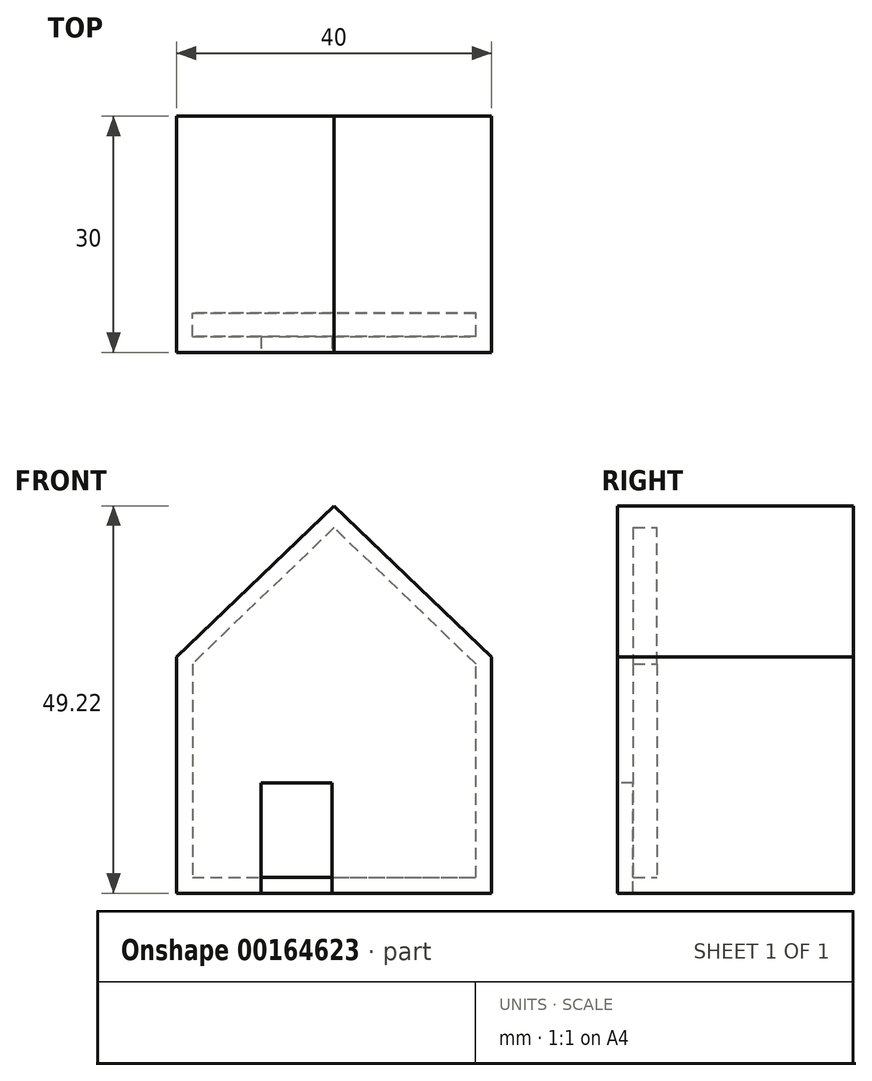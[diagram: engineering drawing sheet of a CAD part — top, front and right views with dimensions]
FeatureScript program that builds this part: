
annotation { "Feature Type Name" : "Feature", "Feature Type Description" : "" }
export const myFeature = defineFeature(function(context is Context, id is Id, definition is map)
    precondition{}
    {
        {
            var Q0;
            Q0=qCreatedBy(makeId("Front.planeOp"),FACE);
            var sketch = newSketch(context, id + "F0", { "sketchPlane" : qUnion([Q0])});
            skLineSegment(sketch, "E0", {"start": v(0, 0) * mm, "end": v(40, 0) * mm});
            skLineSegment(sketch, "E1", {"start": v(40, 0) * mm, "end": v(40, 30) * mm});
            skLineSegment(sketch, "E2", {"start": v(40, 30) * mm, "end": v(20, 49.22) * mm});
            skLineSegment(sketch, "E3", {"start": v(20, 49.22) * mm, "end": v(0, 30) * mm});
            skLineSegment(sketch, "E4", {"start": v(0, 30) * mm, "end": v(0, 0) * mm});
            skSolve(sketch);
        }
        {
            var Q0;
            Q0=makeQuery(id+"F0.imprint","IMPRINT",FACE,{"disambiguationData":[TD([[makeQuery(id+"F0.imprint","IMPRINT",EDGE,{"derivedFrom":sQuery(id+"F0.wireOp",EDGE,"E0")}),1.0]])]});
            extrude(context, id + "F1", {"entities" : qUnion([Q0]), "depth" : 30 * mm});
        }
        {
            var Q0;
            Q0=makeQuery(id+"F1.opExtrude","CAP_FACE",FACE,{"disambiguationData":[OSD([sQuery(id+"F0.wireOp",EDGE,"E0"),sQuery(id+"F0.wireOp",EDGE,"E1"),sQuery(id+"F0.wireOp",EDGE,"E2"),sQuery(id+"F0.wireOp",EDGE,"E3"),sQuery(id+"F0.wireOp",EDGE,"E4")])],"isStart":false});
            var Q1;
            Q1=makeQuery(id+"F1.opExtrude","SWEPT_FACE",FACE,{"disambiguationData":[OSD([sQuery(id+"F0.wireOp",EDGE,"E1")])]});
            var Q2;
            Q2=makeQuery(id+"F1.opExtrude","SWEPT_FACE",FACE,{"disambiguationData":[OSD([sQuery(id+"F0.wireOp",EDGE,"E2")])]});
            var Q3;
            Q3=makeQuery(id+"F1.opExtrude","SWEPT_BODY",BODY,{"disambiguationData":[OSD([sQuery(id+"F0.wireOp",EDGE,"E0"),sQuery(id+"F0.wireOp",EDGE,"E1"),sQuery(id+"F0.wireOp",EDGE,"E2"),sQuery(id+"F0.wireOp",EDGE,"E3"),sQuery(id+"F0.wireOp",EDGE,"E4")])]});
            shell(context, id + "F2", {"isHollow" : true, "entities" : qUnion([Q0, Q1, Q2]), "parts" : qUnion([Q3]), "thickness" : 2 * mm});
        }
        {
            var Q0;
            Q0=makeQuery(id+"F1.opExtrude","CAP_FACE",FACE,{"disambiguationData":[OSD([sQuery(id+"F0.wireOp",EDGE,"E0"),sQuery(id+"F0.wireOp",EDGE,"E1"),sQuery(id+"F0.wireOp",EDGE,"E2"),sQuery(id+"F0.wireOp",EDGE,"E3"),sQuery(id+"F0.wireOp",EDGE,"E4")])],"isStart":false});
            var sketch = newSketch(context, id + "F3", { "sketchPlane" : qUnion([Q0])});
            skLineSegment(sketch, "E5", {"start": v(10.7, 0) * mm, "end": v(10.7, 14) * mm});
            skLineSegment(sketch, "E6", {"start": v(10.7, 14) * mm, "end": v(19.76, 14) * mm});
            skLineSegment(sketch, "E7", {"start": v(19.76, 14) * mm, "end": v(19.76, 0) * mm});
            skSolve(sketch);
        }
        {
            var Q0;
            {var subQ0=sQuery(id+"F3.wireOp",EDGE,"E5");Q0=makeQuery(id+"F3.imprint","IMPRINT",FACE,{"disambiguationData":[TD([[makeQuery(id+"F3.imprint","IMPRINT",EDGE,{"derivedFrom":subQ0}),-1.0]])]});}
            extrude(context, id + "F4", {"entities" : qUnion([Q0]), "operationType" : NewBodyOperationType.REMOVE, "oppositeDirection" : true, "depth" : 2 * mm});
        }
        {
            var Q0;
            Q0 = qSketchRegion(id + "F0", true);
            extrude(context, id + "F5", {"entities" : qUnion([Q0]), "operationType" : NewBodyOperationType.ADD, "depth" : 25 * mm});
        }
    });
